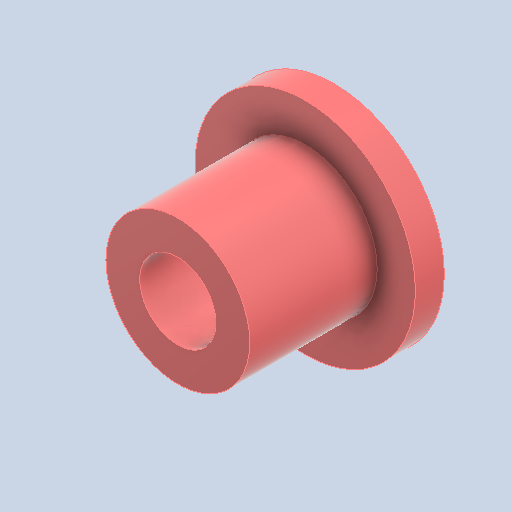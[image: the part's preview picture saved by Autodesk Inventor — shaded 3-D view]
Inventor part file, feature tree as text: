
AUTODESK INVENTOR PART (.ipt)
format: ipt  version: 2022 (Build 260153000, 153)  size: 138,240 bytes
history: native  units: in
note: dims shown in document units (in); Inventor stores cm internally (conversion verified against a paired STEP export)
features: other x3, sketch x2
ambient origin geometry x8: Origin, YZ Plane, XZ Plane, XY Plane, X Axis, Y Axis, Z Axis, Center Point
bodies: Solid1 (feature_tree)
feature tree (5):
  other  "bearingsleeve_MIR.ipt"
  other  "Solid1::bearingsleeve_MIR.ipt"
  other  "TaggingFeature1"
  sketch  "Sketch1"  dims[d0=0.3937in]
  sketch  "Sketch2"
